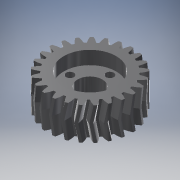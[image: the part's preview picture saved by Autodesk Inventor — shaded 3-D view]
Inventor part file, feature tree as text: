
AUTODESK INVENTOR PART (.ipt)
format: ipt  version: 2018 (Build 220112000, 112)  size: 821,760 bytes
history: native  units: mm (DEFAULTED — no unit token found)
features: sketch x5, other x4, extrude x3, plane x3, mirror x1, hole x1, projected_geometry x1
ambient origin geometry x8: Origin, YZ Plane, XZ Plane, XY Plane, X Axis, Y Axis, Z Axis, Center Point
bodies: Solid1 (feature_tree)
feature tree (18):
  other  "Ground_Tracker_ElevationPinion"
  extrude  "Extrusion1"  Depth=8.0mm TaperAngle=0.0deg
  plane  "Work Plane2"
  plane  "Work Plane8"
  plane  "Work Plane9"
  other  "Spur Gear"
  mirror  "Mirror1"
  extrude  "Extrusion2"  Depth=10.0mm TaperAngle=0.0deg
  extrude  "Extrusion3"  Depth=1.256637mm TaperAngle=0.0deg
  hole  "Hole1"  [1 undecoded]
  sketch  "Sketch1"  dims[d0=41.071448mm d1=8.0mm d2=0.0mm]
  sketch  "Sketch2"  dims[d3=38.250392mm d4=10.0mm d5=0.0mm]
  other  "Srf1"
  sketch  "Sketch3"  dims[d16=48.195494mm d17=0.0mm d34=1.256637mm]
  sketch  "Sketch4"  dims[d39=0.0mm d41=0.0mm]
  sketch  "Sketch5"  dims[d43=48.195494mm d46=48.195494mm d47=0.0mm d48=0.0mm d49=25.6mm d50=6.5mm d51=0.0mm d52=12.0mm d53=8.0mm d54=0.0mm d55=40.0mm d57=360.0deg d59=19.558mm d60=3.797mm d61=6.0mm d62=7.087mm d63=2.0mm d64=14.3117mm d65=8.0mm d66=20.594885mm]
  projected_geometry  "Projected Loop1"
  other  "Pitch Diameter"
note: 1 required parameter value undecoded (feature->parameter linkage not recoverable at this tier; creation-order binding heuristic only, values carry confidence <= 0.55)
